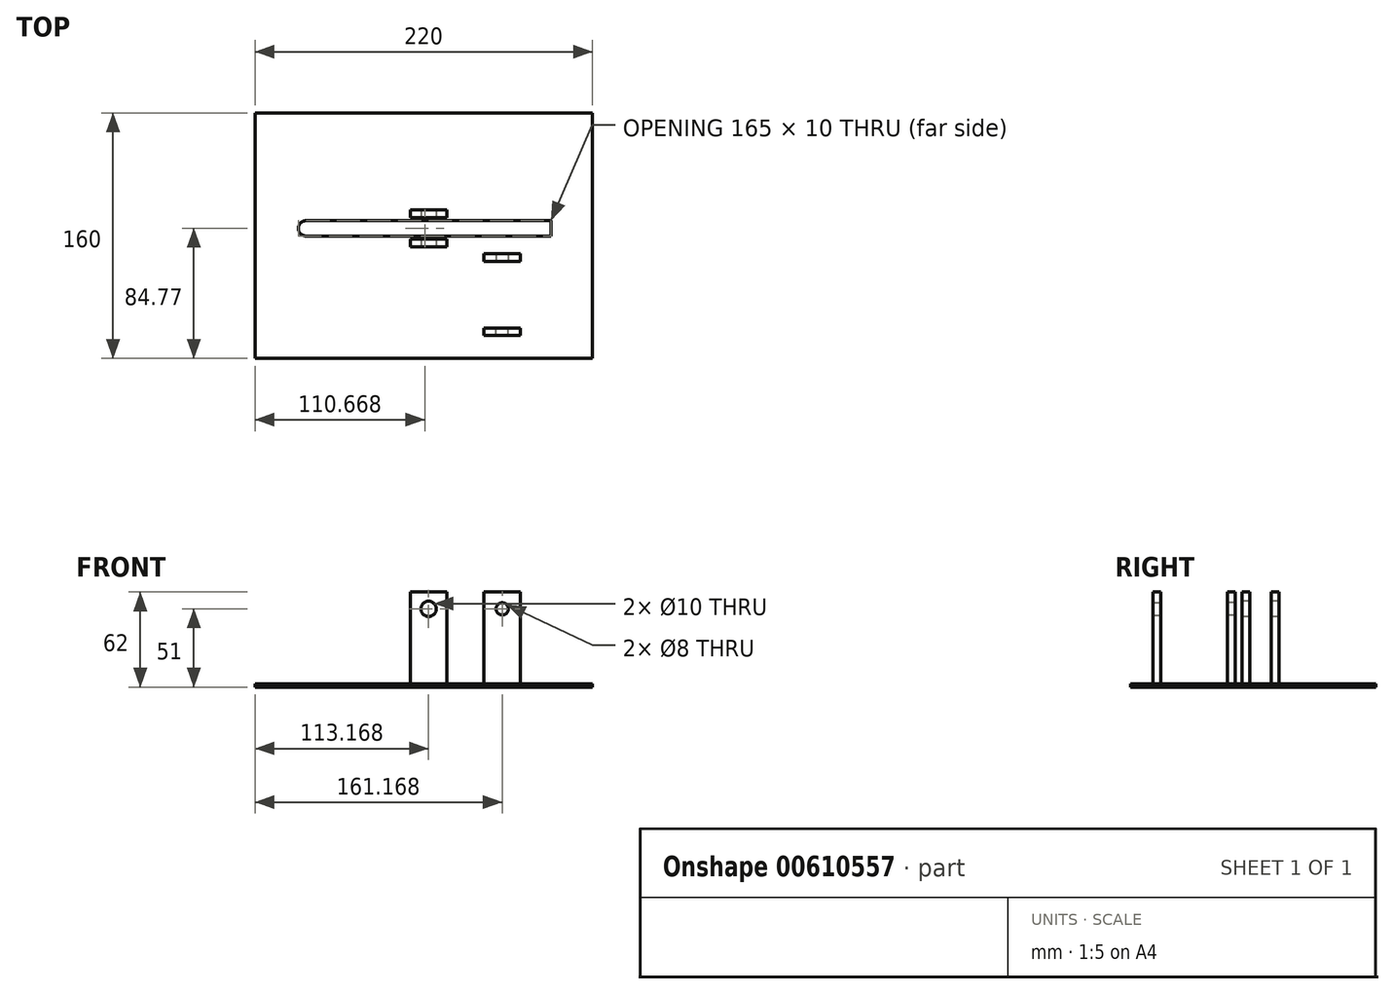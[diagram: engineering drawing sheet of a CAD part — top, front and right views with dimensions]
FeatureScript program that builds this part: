
annotation { "Feature Type Name" : "Feature", "Feature Type Description" : "" }
export const myFeature = defineFeature(function(context is Context, id is Id, definition is map)
    precondition{}
    {
        {
            var Q0;
            Q0=qCreatedBy(makeId("Top.planeOp"),FACE);
            var sketch = newSketch(context, id + "F0", { "sketchPlane" : qUnion([Q0])});
            skLineSegment(sketch, "E0.bottom", {"start": v(-180.89, 75.23) * mm, "end": v(39.11, 75.23) * mm});
            skLineSegment(sketch, "E0.top", {"start": v(-180.89, -84.77) * mm, "end": v(39.11, -84.77) * mm});
            skLineSegment(sketch, "E0.left", {"start": v(-180.89, 75.23) * mm, "end": v(-180.89, -84.77) * mm});
            skLineSegment(sketch, "E0.right", {"start": v(39.11, 75.23) * mm, "end": v(39.11, -84.77) * mm});
            skSolve(sketch);
        }
        {
            var Q0;
            Q0 = qSketchRegion(id + "F0", true);
            extrude(context, id + "F1", {"entities" : qUnion([Q0]), "oppositeDirection" : true, "depth" : 2 * mm, "offsetDistance" : 25 * mm});
        }
        {
            var Q0;
            Q0=makeQuery(id+"F1.opExtrude","CAP_FACE",FACE,{"disambiguationData":[OSD([sQuery(id+"F0.wireOp",EDGE,"E0.bottom"),sQuery(id+"F0.wireOp",EDGE,"E0.top"),sQuery(id+"F0.wireOp",EDGE,"E0.left"),sQuery(id+"F0.wireOp",EDGE,"E0.right")])],"isStart":true});
            var sketch = newSketch(context, id + "F2", { "sketchPlane" : qUnion([Q0])});
            skLineSegment(sketch, "E1", {"start": v(12.28, 5) * mm, "end": v(-147.72, 5) * mm});
            skLineSegment(sketch, "E2", {"start": v(12.28, -5) * mm, "end": v(-147.72, -5) * mm});
            skArc(sketch, "E3", {"start": v(-147.72, 5) * mm, "mid": v(-152.72, 0) * mm, "end": v(-147.72, -5) * mm});
            skLineSegment(sketch, "E4", {"start": v(12.28, 5) * mm, "end": v(12.28, -5) * mm});
            skSolve(sketch);
        }
        {
            var Q0;
            Q0=makeQuery(id+"F2.imprint","IMPRINT",FACE,{"disambiguationData":[TD([[makeQuery(id+"F2.imprint","IMPRINT",EDGE,{"derivedFrom":sQuery(id+"F2.wireOp",EDGE,"E1")}),1.0]])]});
            extrude(context, id + "F3", {"entities" : qUnion([Q0]), "operationType" : NewBodyOperationType.REMOVE, "oppositeDirection" : true, "depth" : 25 * mm, "offsetDistance" : 25 * mm});
        }
        {
            var Q0;
            Q0=makeQuery(id+"F1.opExtrude","CAP_FACE",FACE,{"disambiguationData":[OSD([sQuery(id+"F0.wireOp",EDGE,"E0.bottom"),sQuery(id+"F0.wireOp",EDGE,"E0.top"),sQuery(id+"F0.wireOp",EDGE,"E0.left"),sQuery(id+"F0.wireOp",EDGE,"E0.right")])],"isStart":true});
            var sketch = newSketch(context, id + "F4", { "sketchPlane" : qUnion([Q0])});
            skLineSegment(sketch, "E5.bottom", {"start": v(-79.72, -7) * mm, "end": v(-55.72, -7) * mm});
            skLineSegment(sketch, "E5.top", {"start": v(-79.72, -12) * mm, "end": v(-55.72, -12) * mm});
            skLineSegment(sketch, "E5.left", {"start": v(-79.72, -7) * mm, "end": v(-79.72, -12) * mm});
            skLineSegment(sketch, "E5.right", {"start": v(-55.72, -7) * mm, "end": v(-55.72, -12) * mm});
            skLineSegment(sketch, "E6.MirrorCS", {"start": v(-55.72, 7) * mm, "end": v(-55.72, 12) * mm});
            skLineSegment(sketch, "E7.MirrorCS", {"start": v(-79.72, 7) * mm, "end": v(-79.72, 12) * mm});
            skLineSegment(sketch, "E8.MirrorCS", {"start": v(-79.72, 7) * mm, "end": v(-55.72, 7) * mm});
            skLineSegment(sketch, "E9.MirrorCS", {"start": v(-79.72, 12) * mm, "end": v(-55.72, 12) * mm});
            skSolve(sketch);
        }
        {
            var Q0;
            Q0 = qSketchRegion(id + "F4", true);
            extrude(context, id + "F5", {"entities" : qUnion([Q0]), "operationType" : NewBodyOperationType.ADD, "depth" : 60 * mm, "offsetDistance" : 25 * mm});
        }
        {
            var Q0;
            Q0=makeQuery(id+"F5.opExtrude","SWEPT_FACE",FACE,{"disambiguationData":[OSD([sQuery(id+"F4.wireOp",EDGE,"E5.top")])]});
            var sketch = newSketch(context, id + "F6", { "sketchPlane" : qUnion([Q0])});
            skCircle(sketch, "E10", {"center": v(-67.72, 49) * mm, "radius": 5 * mm});
            skPoint(sketch, "E10.centerSnap0", {"position": v(-67.72, 60) * mm});
            skSolve(sketch);
        }
        {
            var Q0;
            Q0 = qSketchRegion(id + "F6", true);
            extrude(context, id + "F7", {"entities" : qUnion([Q0]), "operationType" : NewBodyOperationType.REMOVE, "oppositeDirection" : true, "depth" : 25 * mm, "offsetDistance" : 25 * mm});
        }
        {
            var Q0;
            Q0=makeQuery(id+"F2.imprint","IMPRINT",FACE,{"disambiguationData":[TD([[makeQuery(id+"F2.imprint","IMPRINT",EDGE,{"derivedFrom":sQuery(id+"F2.wireOp",EDGE,"E1")}),-1.0]])]});
            var sketch = newSketch(context, id + "F8", { "sketchPlane" : qUnion([Q0])});
            skLineSegment(sketch, "E11.bottom", {"start": v(-31.72, -16.5) * mm, "end": v(-7.72, -16.5) * mm});
            skLineSegment(sketch, "E11.top", {"start": v(-31.72, -21.5) * mm, "end": v(-7.72, -21.5) * mm});
            skLineSegment(sketch, "E11.left", {"start": v(-31.72, -16.5) * mm, "end": v(-31.72, -21.5) * mm});
            skLineSegment(sketch, "E11.right", {"start": v(-7.72, -16.5) * mm, "end": v(-7.72, -21.5) * mm});
            skLineSegment(sketch, "E12.bottom", {"start": v(-31.72, -65) * mm, "end": v(-7.72, -65) * mm});
            skLineSegment(sketch, "E12.top", {"start": v(-31.72, -70) * mm, "end": v(-7.72, -70) * mm});
            skLineSegment(sketch, "E12.left", {"start": v(-31.72, -65) * mm, "end": v(-31.72, -70) * mm});
            skLineSegment(sketch, "E12.right", {"start": v(-7.72, -65) * mm, "end": v(-7.72, -70) * mm});
            skSolve(sketch);
        }
        {
            var Q0;
            Q0 = qSketchRegion(id + "F8", true);
            extrude(context, id + "F9", {"entities" : qUnion([Q0]), "operationType" : NewBodyOperationType.ADD, "depth" : 60 * mm, "offsetDistance" : 25 * mm});
        }
        {
            var Q0;
            Q0=makeQuery(id+"F9.opExtrude","SWEPT_FACE",FACE,{"disambiguationData":[OSD([sQuery(id+"F8.wireOp",EDGE,"E11.top")])]});
            var sketch = newSketch(context, id + "F10", { "sketchPlane" : qUnion([Q0])});
            skCircle(sketch, "E13", {"center": v(-19.72, 49) * mm, "radius": 4 * mm});
            skPoint(sketch, "E13.centerSnap0", {"position": v(-19.72, 60) * mm});
            skSolve(sketch);
        }
        {
            var Q0;
            Q0=makeQuery(id+"F10.imprint","IMPRINT",FACE,{"disambiguationData":[TD([[makeQuery(id+"F10.imprint","IMPRINT",EDGE,{"derivedFrom":sQuery(id+"F10.wireOp",EDGE,"E13")}),1.0]])]});
            var Q1;
            Q1=sQuery(id+"F10.wireOp",EDGE,"E13");
            extrude(context, id + "F11", {"entities" : qUnion([Q0]), "operationType" : NewBodyOperationType.REMOVE, "surfaceEntities" : qUnion([Q1]), "oppositeDirection" : true, "depth" : 25 * mm, "offsetDistance" : 25 * mm});
        }
        {
            var Q0;
            Q0 = qSketchRegion(id + "F10", true);
            extrude(context, id + "F12", {"entities" : qUnion([Q0]), "operationType" : NewBodyOperationType.REMOVE, "depth" : 100 * mm, "offsetDistance" : 25 * mm});
        }
    });
